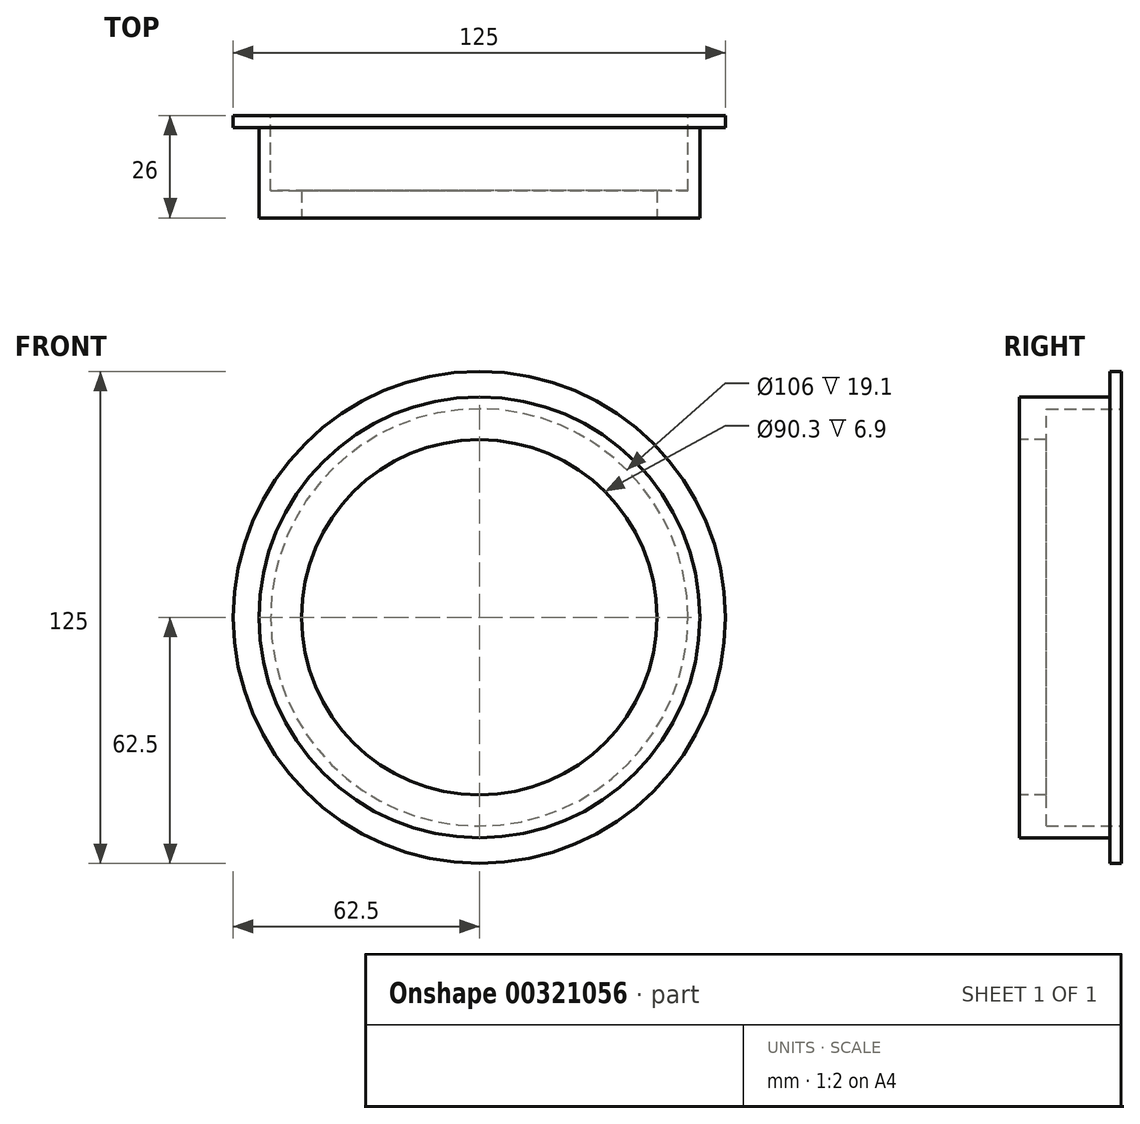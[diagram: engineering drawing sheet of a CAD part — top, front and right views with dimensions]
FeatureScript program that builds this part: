
annotation { "Feature Type Name" : "Feature", "Feature Type Description" : "" }
export const myFeature = defineFeature(function(context is Context, id is Id, definition is map)
    precondition{}
    {
        {
            var Q0;
            Q0=qCreatedBy(makeId("Front.planeOp"),FACE);
            var sketch = newSketch(context, id + "F0", { "sketchPlane" : qUnion([Q0])});
            skCircle(sketch, "E0", {"center": v(0, 0) * mm, "radius": 56 * mm});
            skCircle(sketch, "E1", {"center": v(0, 0) * mm, "radius": 53 * mm});
            skSolve(sketch);
        }
        {
            var Q0;
            Q0=qSketchRegion(id+"F0",true);
            extrude(context, id + "F1", {"entities" : qUnion([Q0]), "depth" : 20 * mm});
        }
        {
            var Q0;
            Q0=makeQuery(id+"F1.opExtrude","CAP_FACE",FACE,{"disambiguationData":[OSD([sQuery(id+"F0.wireOp",EDGE,"E0"),sQuery(id+"F0.wireOp",EDGE,"E1")])],"isStart":false});
            var sketch = newSketch(context, id + "F2", { "sketchPlane" : qUnion([Q0])});
            skCircle(sketch, "E2", {"center": v(0, 0) * mm, "radius": 56 * mm});
            skCircle(sketch, "E3", {"center": v(0, 0) * mm, "radius": 45.15 * mm});
            skSolve(sketch);
        }
        {
            var Q0;
            Q0 = qSketchRegion(id + "F2", true);
            extrude(context, id + "F3", {"entities" : qUnion([Q0]), "operationType" : NewBodyOperationType.ADD, "oppositeDirection" : true, "depth" : 6.9 * mm});
        }
        {
            var Q0;
            Q0=makeQuery(id+"F1.opExtrude","CAP_FACE",FACE,{"disambiguationData":[OSD([sQuery(id+"F0.wireOp",EDGE,"E0"),sQuery(id+"F0.wireOp",EDGE,"E1")])],"isStart":true});
            var sketch = newSketch(context, id + "F4", { "sketchPlane" : qUnion([Q0])});
            skCircle(sketch, "E4", {"center": v(0, 0) * mm, "radius": 53 * mm});
            skCircle(sketch, "E5", {"center": v(0, 0) * mm, "radius": 56 * mm});
            skSolve(sketch);
        }
        {
            var Q0;
            Q0 = qSketchRegion(id + "F4", true);
            extrude(context, id + "F5", {"entities" : qUnion([Q0]), "operationType" : NewBodyOperationType.ADD, "depth" : 3 * mm});
        }
        {
            var Q0;
            Q0=makeQuery(id+"F5.opExtrude","CAP_FACE",FACE,{"disambiguationData":[OSD([sQuery(id+"F4.wireOp",EDGE,"E4"),sQuery(id+"F4.wireOp",EDGE,"E5")])],"isStart":false});
            var sketch = newSketch(context, id + "F6", { "sketchPlane" : qUnion([Q0])});
            skCircle(sketch, "E6", {"center": v(0, 0) * mm, "radius": 53 * mm});
            skCircle(sketch, "E7", {"center": v(0, 0) * mm, "radius": 62.5 * mm});
            skSolve(sketch);
        }
        {
            var Q0;
            Q0 = qSketchRegion(id + "F6", true);
            extrude(context, id + "F7", {"entities" : qUnion([Q0]), "operationType" : NewBodyOperationType.ADD, "depth" : 3 * mm});
        }
    });
